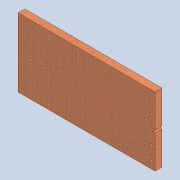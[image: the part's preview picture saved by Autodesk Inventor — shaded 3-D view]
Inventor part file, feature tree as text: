
AUTODESK INVENTOR PART (.ipt)
format: ipt  version: 2020 (Build 240168000, 168)  size: 144,384 bytes
history: native  units: mm
features: sketch x3, hole x2, pattern_linear x2, extrude x1
ambient origin geometry x8: Origin, YZ Plane, XZ Plane, XY Plane, X Axis, Y Axis, Z Axis, Center Point
bodies: Solid1 (feature_tree)
feature tree (8):
  extrude  "Extrusion1"  Depth=200.0mm
  hole  "Hole1"  [1 undecoded]
  pattern_linear  "Rectangular Pattern1"  Count1=2  [1 undecoded]
  hole  "Hole2"  [1 undecoded]
  pattern_linear  "Rectangular Pattern2"  Count1=5  [1 undecoded]
  sketch  "Sketch1"  dims[d0=400.0mm d1=200.0mm]
  sketch  "Sketch10"  dims[d2=20.0mm d3=0.0mm]
  sketch  "Sketch11"  dims[d46=8.0mm d47=6.0mm d48=4.0mm d49=2.0mm d50=90.0deg d51=8.0mm d52=20.594885mm d53=40.0mm d54=20.0mm d56=40.0mm d57=10.0mm d58=8.0mm d59=6.0mm d60=4.0mm d61=2.0mm d62=90.0deg d63=8.0mm d64=20.594885mm d65=50.0mm d67=40.0mm d68=20.0mm d70=180.0mm]
note: 4 required parameter values undecoded (feature->parameter linkage not recoverable at this tier; creation-order binding heuristic only, values carry confidence <= 0.55)
